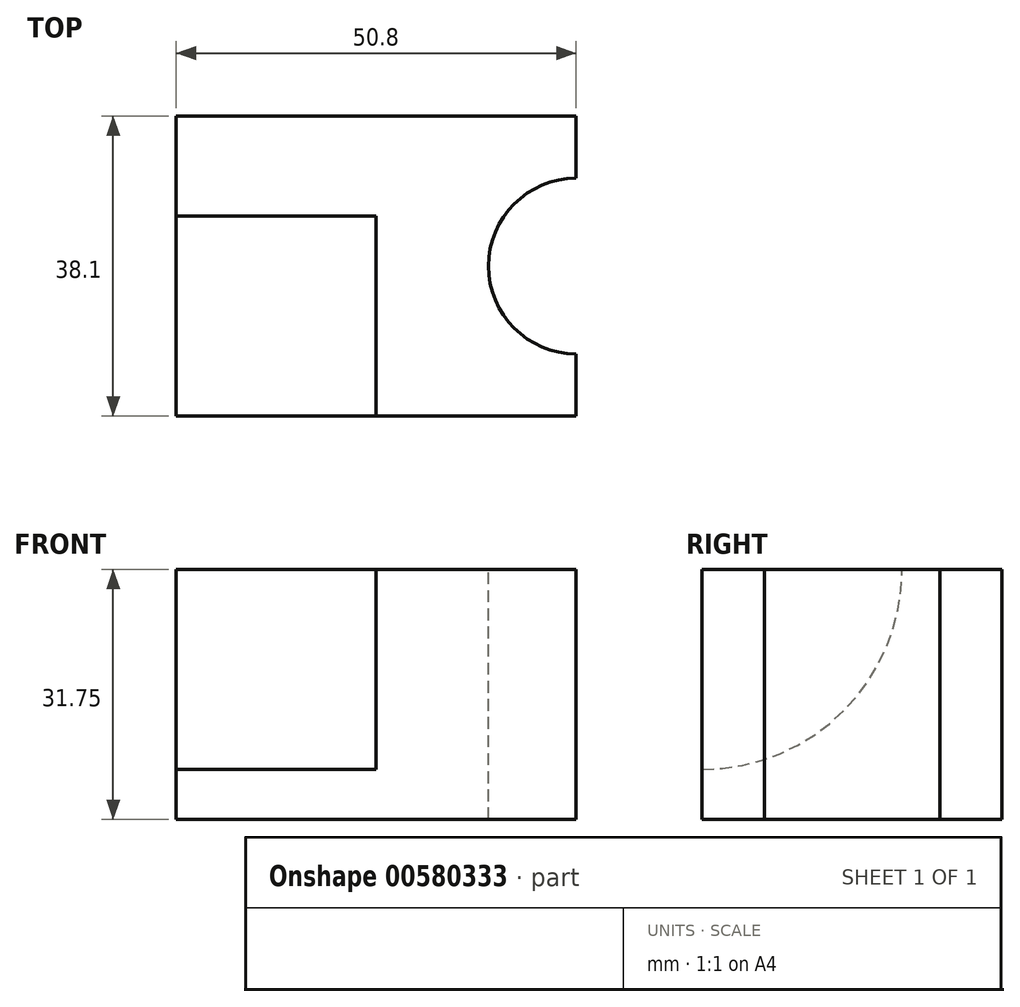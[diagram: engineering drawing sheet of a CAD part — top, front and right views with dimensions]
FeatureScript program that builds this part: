
annotation { "Feature Type Name" : "Feature", "Feature Type Description" : "" }
export const myFeature = defineFeature(function(context is Context, id is Id, definition is map)
    precondition{}
    {
        {
            var Q0;
            Q0=qCreatedBy(makeId("Front.planeOp"),FACE);
            var sketch = newSketch(context, id + "F0", { "sketchPlane" : qUnion([Q0])});
            skLineSegment(sketch, "E0", {"start": v(0, 0) * mm, "end": v(50.8, 0) * mm});
            skLineSegment(sketch, "E1", {"start": v(50.8, 0) * mm, "end": v(50.8, 31.75) * mm});
            skLineSegment(sketch, "E2", {"start": v(50.8, 31.75) * mm, "end": v(0, 31.75) * mm});
            skLineSegment(sketch, "E3", {"start": v(0, 31.75) * mm, "end": v(0, 0) * mm});
            skSolve(sketch);
        }
        {
            var Q0;
            Q0=makeQuery(id+"F0.imprint","IMPRINT",FACE,{"disambiguationData":[TD([[makeQuery(id+"F0.imprint","IMPRINT",EDGE,{"derivedFrom":sQuery(id+"F0.wireOp",EDGE,"E0")}),1.0]])]});
            extrude(context, id + "F1", {"entities" : qUnion([Q0]), "depth" : 38.1 * mm, "offsetDistance" : 25.4 * mm});
        }
        {
            var Q0;
            Q0=makeQuery(id+"F1.opExtrude","SWEPT_FACE",FACE,{"disambiguationData":[OSD([sQuery(id+"F0.wireOp",EDGE,"E2")])]});
            var sketch = newSketch(context, id + "F2", { "sketchPlane" : qUnion([Q0])});
            skCircle(sketch, "E4", {"center": v(50.8, -19.05) * mm, "radius": 11.15 * mm});
            skSolve(sketch);
        }
        {
            var Q0;
            {var subQ0=sQuery(id+"F2.wireOp",EDGE,"E4");var subQ1=makeQuery(id+"F1.opExtrude","SWEPT_EDGE",EDGE,{"disambiguationData":[OSD([sQuery(id+"F0.wireOp",EDGE,"E1"),sQuery(id+"F0.wireOp",EDGE,"E2")])]});var subQ2=makeQuery(id+"F2.imprint","INTERSECT",VERTEX,{"disambiguationData":[OD(0.0)],"derivedFrom":[subQ1,subQ0]});Q0=makeQuery(id+"F2.imprint","IMPRINT",FACE,{"disambiguationData":[TD([[makeQuery(id+"F2.imprint","IMPRINT",EDGE,{"disambiguationData":[TD([[subQ2,-1.0]])],"derivedFrom":subQ0}),1.0]])]});}
            extrude(context, id + "F3", {"entities" : qUnion([Q0]), "operationType" : NewBodyOperationType.REMOVE, "oppositeDirection" : true, "depth" : 31.75 * mm, "offsetDistance" : 25.4 * mm});
        }
        {
            var Q0;
            Q0=makeQuery(id+"F1.opExtrude","SWEPT_FACE",FACE,{"disambiguationData":[OSD([sQuery(id+"F0.wireOp",EDGE,"E3")])]});
            var sketch = newSketch(context, id + "F4", { "sketchPlane" : qUnion([Q0])});
            skLineSegment(sketch, "E5", {"start": v(0, 31.75) * mm, "end": v(12.7, 31.75) * mm});
            skLineSegment(sketch, "E6", {"start": v(38.1, 0) * mm, "end": v(38.1, 6.35) * mm});
            skArc(sketch, "E7", {"start": v(12.7, 31.75) * mm, "mid": v(20.14, 13.79) * mm, "end": v(38.1, 6.35) * mm});
            skSolve(sketch);
        }
        {
            var Q0;
            {var subQ0=sQuery(id+"F4.wireOp",EDGE,"E7");Q0=makeQuery(id+"F4.imprint","IMPRINT",FACE,{"disambiguationData":[TD([[makeQuery(id+"F4.imprint","IMPRINT",EDGE,{"derivedFrom":subQ0}),1.0]])]});}
            extrude(context, id + "F5", {"entities" : qUnion([Q0]), "operationType" : NewBodyOperationType.REMOVE, "oppositeDirection" : true, "depth" : 25.4 * mm, "offsetDistance" : 25.4 * mm});
        }
    });
